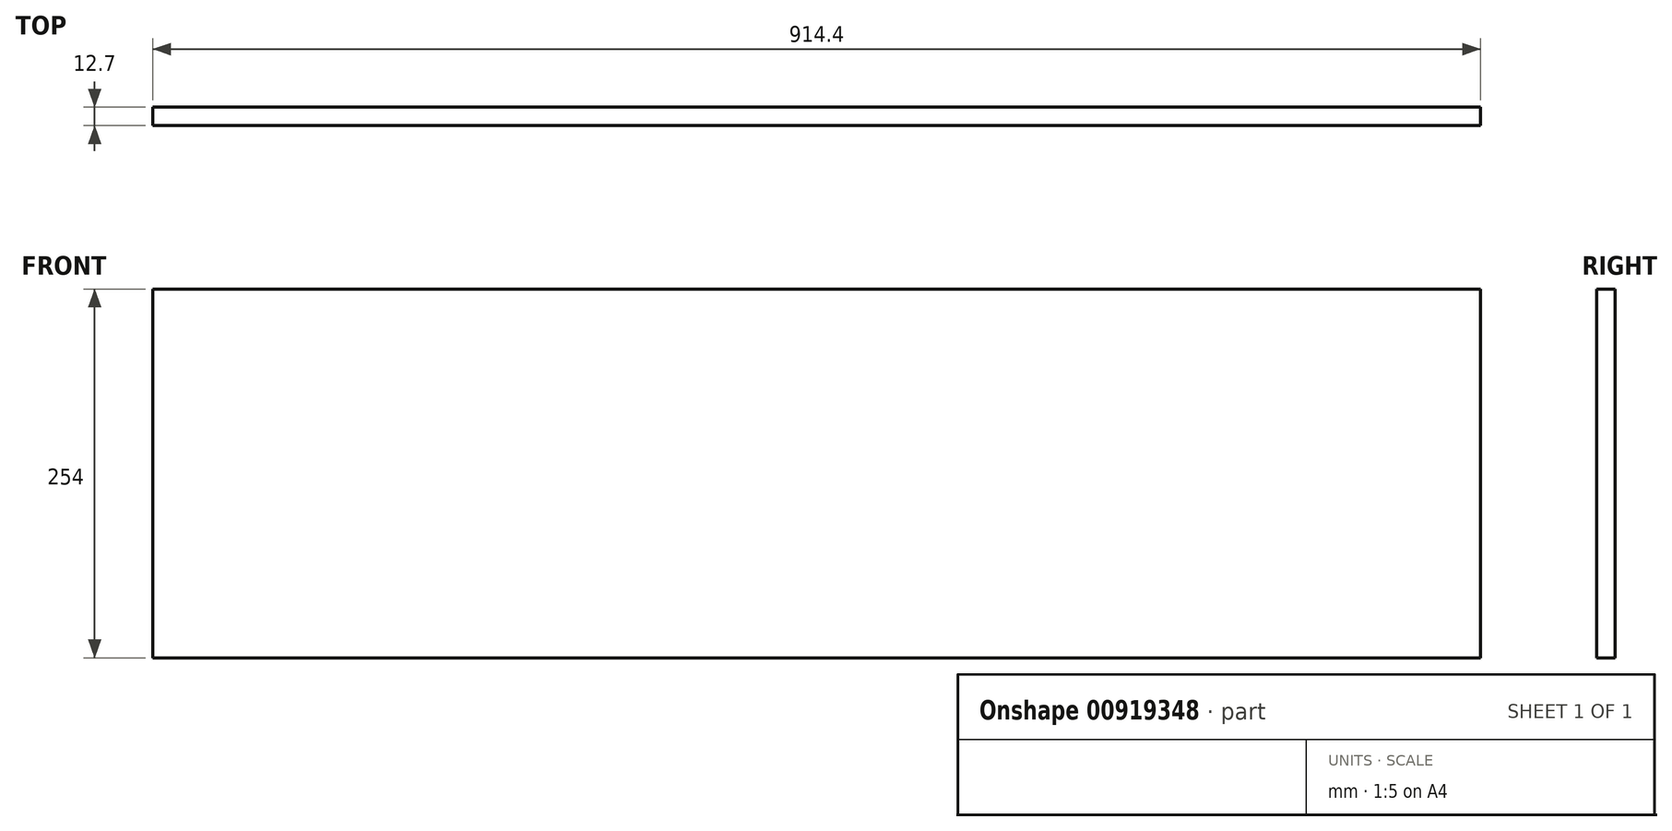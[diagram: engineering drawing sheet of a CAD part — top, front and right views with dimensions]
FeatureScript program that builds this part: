
annotation { "Feature Type Name" : "Feature", "Feature Type Description" : "" }
export const myFeature = defineFeature(function(context is Context, id is Id, definition is map)
    precondition{}
    {
        {
            var Q0;
            Q0=qCreatedBy(makeId("Front.planeOp"),FACE);
            var sketch = newSketch(context, id + "F0", { "sketchPlane" : qUnion([Q0])});
            skLineSegment(sketch, "E0.bottom", {"start": v(457.2, -127) * mm, "end": v(-457.2, -127) * mm});
            skLineSegment(sketch, "E0.top", {"start": v(457.2, 127) * mm, "end": v(-457.2, 127) * mm});
            skLineSegment(sketch, "E0.left", {"start": v(457.2, -127) * mm, "end": v(457.2, 127) * mm});
            skLineSegment(sketch, "E0.right", {"start": v(-457.2, -127) * mm, "end": v(-457.2, 127) * mm});
            skPoint(sketch, "E0.middle", {"position": v(0, 0) * mm});
            skSolve(sketch);
        }
        {
            var Q0;
            Q0=makeQuery(id+"F0.imprint","IMPRINT",FACE,{"disambiguationData":[TD([[makeQuery(id+"F0.imprint","IMPRINT",EDGE,{"derivedFrom":sQuery(id+"F0.wireOp",EDGE,"E0.bottom")}),-1.0]])]});
            extrude(context, id + "F1", {"entities" : qUnion([Q0]), "depth" : 12.7 * mm, "offsetDistance" : 25.4 * mm});
        }
    });
